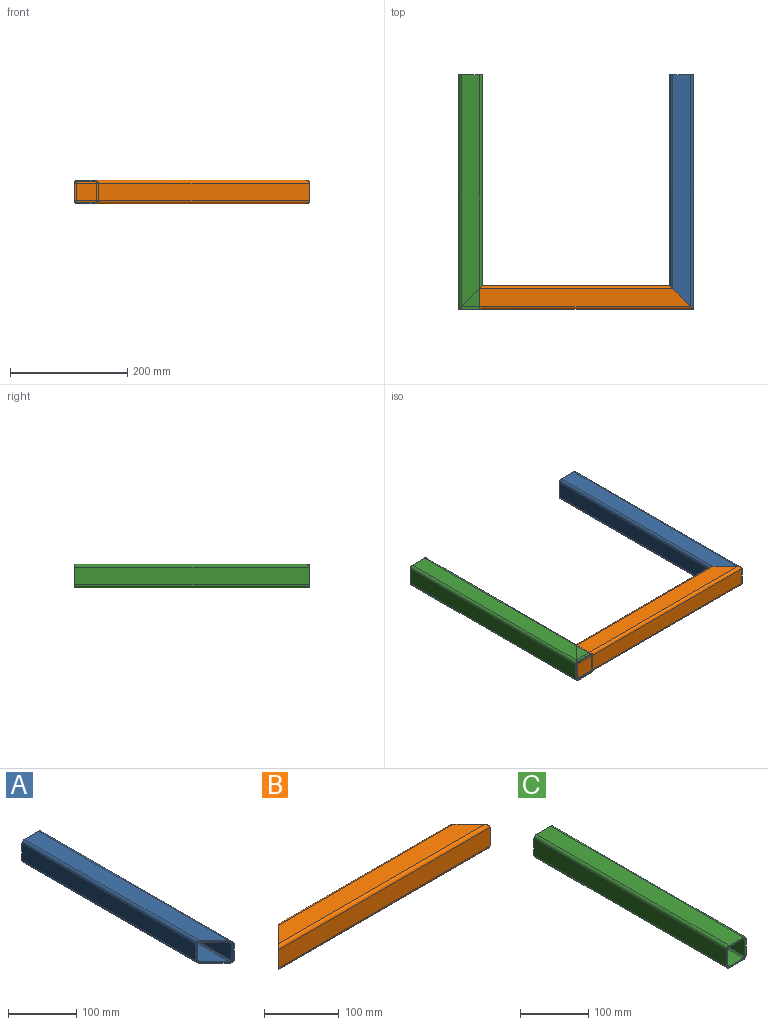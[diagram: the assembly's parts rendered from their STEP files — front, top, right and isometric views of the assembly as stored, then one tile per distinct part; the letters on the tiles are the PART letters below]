
ASSEMBLY  parts=3 mates=1
PART A: 18 faces, bbox 40x400x40 mm
  f0: plane 395x30mm, normal (0,0,1), area 11400mm2, adj f2,f3,f16,f17
  f1: plane 360x30mm, normal (-1,0,0), area 10800mm2, adj f3,f4,f16,f17
  f2: cylinder r=5mm len=400mm, axis (0,1,0), area 3127.3mm2, adj f0,f15,f16,f17
  f3: cylinder r=5mm len=365mm, axis (0,1,0), area 2841.7mm2, adj f0,f1,f16,f17
  f4: cylinder r=5mm len=365mm, axis (0,1,0), area 2841.7mm2, adj f1,f5,f16,f17
  f5: plane 395x30mm, normal (0,0,-1), area 11400mm2, adj f4,f14,f16,f17
  f6: cylinder r=2.5mm len=365mm, axis (0,1,0), area 1427.1mm2, adj f7,f13,f16,f17
  f7: plane 395x30mm, normal (0,0,-1), area 11400mm2, adj f6,f8,f16,f17
  f8: cylinder r=2.5mm len=397.5mm, axis (0,1,0), area 1557.4mm2, adj f7,f9,f16,f17
  f9: plane 397.5x30mm, normal (-1,0,0), area 11925mm2, adj f8,f10,f16,f17
  f10: cylinder r=2.5mm len=397.5mm, axis (0,1,0), area 1557.4mm2, adj f9,f11,f16,f17
  f11: plane 395x30mm, normal (0,0,1), area 11400mm2, adj f10,f12,f16,f17
  f12: cylinder r=2.5mm len=365mm, axis (0,1,0), area 1427.1mm2, adj f11,f13,f16,f17
  f13: plane 362.5x30mm, normal (1,0,0), area 10875mm2, adj f6,f12,f16,f17
  f14: cylinder r=5mm len=400mm, axis (0,1,0), area 3127.3mm2, adj f5,f15,f16,f17
  f15: plane 400x30mm, normal (1,0,0), area 12000mm2, adj f2,f14,f16,f17
  f16: plane 40x40mm, normal (0,1,0), area 358.9mm2, adj f0,f1,f2,f3,f4,f5,f6,f7
  f17: plane 40x40mm, normal (-0.71,-0.71,0), area 507.6mm2, adj f0,f1,f2,f3,f4,f5,f6,f7
PART B: 18 faces, bbox 400x40x40 mm
  f0: cylinder r=5mm len=400mm, axis (-1,0,0), area 3113.1mm2, adj f2,f7,f8,f9
  f1: cylinder r=5mm len=330mm, axis (-1,0,0), area 2541.8mm2, adj f2,f6,f8,f9
  f2: plane 390x30mm, normal (0,0,1), area 10800mm2, adj f0,f1,f8,f9
  f3: cylinder r=5mm len=400mm, axis (-1,0,0), area 3113.1mm2, adj f5,f7,f8,f9
  f4: cylinder r=5mm len=330mm, axis (-1,0,0), area 2541.8mm2, adj f5,f6,f8,f9
  f5: plane 390x30mm, normal (0,0,-1), area 10800mm2, adj f3,f4,f8,f9
  f6: plane 320x30mm, normal (0,1,0), area 9600mm2, adj f1,f4,f8,f9
  f7: plane 400x30mm, normal (0,-1,0), area 12000mm2, adj f0,f3,f8,f9
  f8: plane 40x40mm, normal (0.71,0.71,0), area 507.6mm2, adj f0,f1,f2,f3,f4,f5,f6,f7
  f9: plane 40x40mm, normal (-0.71,0.71,0), area 507.6mm2, adj f0,f1,f2,f3,f4,f5,f6,f7
  f10: cylinder r=2.5mm len=395mm, axis (-1,0,0), area 1544mm2, adj f8,f9,f11,f17
  f11: plane 390x30mm, normal (0,0,-1), area 10800mm2, adj f8,f9,f10,f12
  f12: cylinder r=2.5mm len=330mm, axis (-1,0,0), area 1283.4mm2, adj f8,f9,f11,f13
  f13: plane 325x30mm, normal (0,-1,0), area 9750mm2, adj f8,f9,f12,f14
  f14: cylinder r=2.5mm len=330mm, axis (-1,0,0), area 1283.4mm2, adj f8,f9,f13,f15
  f15: plane 390x30mm, normal (0,0,1), area 10800mm2, adj f8,f9,f14,f16
  f16: cylinder r=2.5mm len=395mm, axis (-1,0,0), area 1544mm2, adj f8,f9,f15,f17
  f17: plane 395x30mm, normal (0,1,0), area 11850mm2, adj f8,f9,f10,f16
PART C: 18 faces, bbox 40x400x40 mm
  f0: cylinder r=5mm len=400mm, axis (0,1,0), area 3141.6mm2, adj f4,f5,f8,f17
  f1: cylinder r=5mm len=400mm, axis (0,1,0), area 3141.6mm2, adj f5,f7,f8,f17
  f2: cylinder r=5mm len=400mm, axis (0,1,0), area 3141.6mm2, adj f6,f7,f8,f17
  f3: cylinder r=5mm len=400mm, axis (0,1,0), area 3141.6mm2, adj f4,f6,f8,f17
  f4: plane 400x30mm, normal (1,0,0), area 12000mm2, adj f0,f3,f8,f17
  f5: plane 400x30mm, normal (0,0,1), area 12000mm2, adj f0,f1,f8,f17
  f6: plane 400x30mm, normal (0,0,-1), area 12000mm2, adj f2,f3,f8,f17
  f7: plane 400x30mm, normal (-1,0,0), area 12000mm2, adj f1,f2,f8,f17
  f8: plane 40x40mm, normal (0,1,0), area 358.9mm2, adj f0,f1,f2,f3,f4,f5,f6,f7
  f9: plane 400x30mm, normal (1,0,0), area 12000mm2, adj f8,f10,f16,f17
  f10: cylinder r=2.5mm len=400mm, axis (0,1,0), area 1570.8mm2, adj f8,f9,f11,f17
  f11: plane 400x30mm, normal (0,0,1), area 12000mm2, adj f8,f10,f12,f17
  f12: cylinder r=2.5mm len=400mm, axis (0,1,0), area 1570.8mm2, adj f8,f11,f13,f17
  f13: plane 400x30mm, normal (-1,0,0), area 12000mm2, adj f8,f12,f14,f17
  f14: cylinder r=2.5mm len=400mm, axis (0,1,0), area 1570.8mm2, adj f8,f13,f15,f17
  f15: plane 400x30mm, normal (0,0,-1), area 12000mm2, adj f8,f14,f16,f17
  f16: cylinder r=2.5mm len=400mm, axis (0,1,0), area 1570.8mm2, adj f8,f9,f15,f17
  f17: plane 40x40mm, normal (0,-1,0), area 358.9mm2, adj f0,f1,f2,f3,f4,f5,f6,f7
PLACE A t=(113.21,475.49,-165.45)mm
PLACE B t=(-190.33,228.02,-42.18)mm
PLACE C t=(-190.33,475.49,-143.91)mm
MATE fastened B.f8 <-> A.f17  axis (0.71,0.71,0) through (204.67,80.49,-143.91)mm
